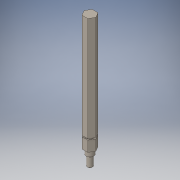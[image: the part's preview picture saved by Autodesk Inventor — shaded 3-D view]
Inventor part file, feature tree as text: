
AUTODESK INVENTOR PART (.ipt)
format: ipt  version: 2016 (Build 200138000, 138)  size: 151,552 bytes
history: native  units: in
note: dims shown in document units (in); Inventor stores cm internally (conversion verified against a paired STEP export)
features: reference x4, extrude x2, sketch x2, plane x1, chamfer x1
ambient origin geometry x8: Origin, YZ Plane, XZ Plane, XY Plane, X Axis, Y Axis, Z Axis, Center Point
bodies: Solid1 (feature_tree)
feature tree (10):
  plane  "Work Plane1"
  extrude  "Extrusion1"  Depth=1.0in TaperAngle=0.0deg
  extrude  "Extrusion2"  [1 undecoded]
  sketch  "Sketch1"  dims[d0=1.0in d1=0.0in d2=0.903in d3=0.0in]
  reference  "Reference1"
  reference  "Reference2"
  reference  "Reference3"
  reference  "Reference4"
  sketch  "Sketch2"
  chamfer  "Chamfer1"  [1 undecoded]
note: 2 required parameter values undecoded (feature->parameter linkage not recoverable at this tier; creation-order binding heuristic only, values carry confidence <= 0.55)
